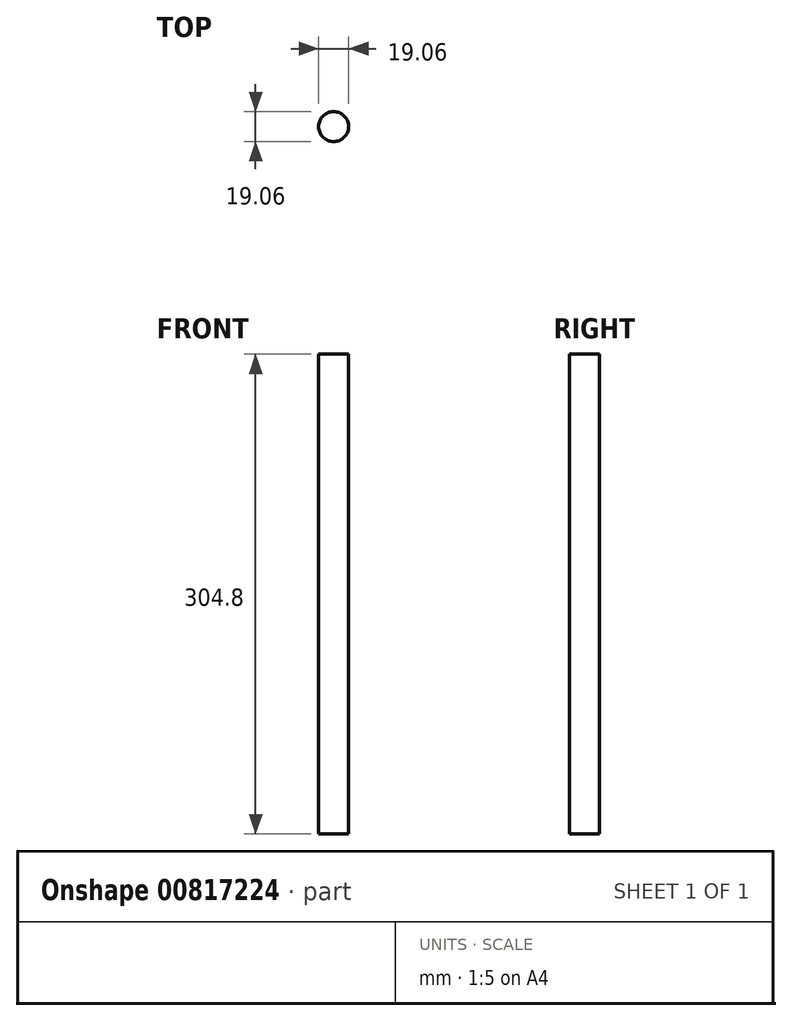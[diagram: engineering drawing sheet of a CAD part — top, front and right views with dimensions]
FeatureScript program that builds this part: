
annotation { "Feature Type Name" : "Feature", "Feature Type Description" : "" }
export const myFeature = defineFeature(function(context is Context, id is Id, definition is map)
    precondition{}
    {
        {
            var Q0;
            Q0=qCreatedBy(makeId("Top.planeOp"),FACE);
            var sketch = newSketch(context, id + "F0", { "sketchPlane" : qUnion([Q0])});
            skCircle(sketch, "E0", {"center": v(0, 0) * mm, "radius": 9.53 * mm});
            skSolve(sketch);
        }
        {
            var Q0;
            Q0=sQuery(id+"F0.wireOp",EDGE,"E0");
            extrude(context, id + "F1", {"bodyType" : ToolBodyType.SURFACE, "surfaceEntities" : qUnion([Q0]), "depth" : 304.8 * mm, "offsetDistance" : 25.4 * mm});
        }
    });
